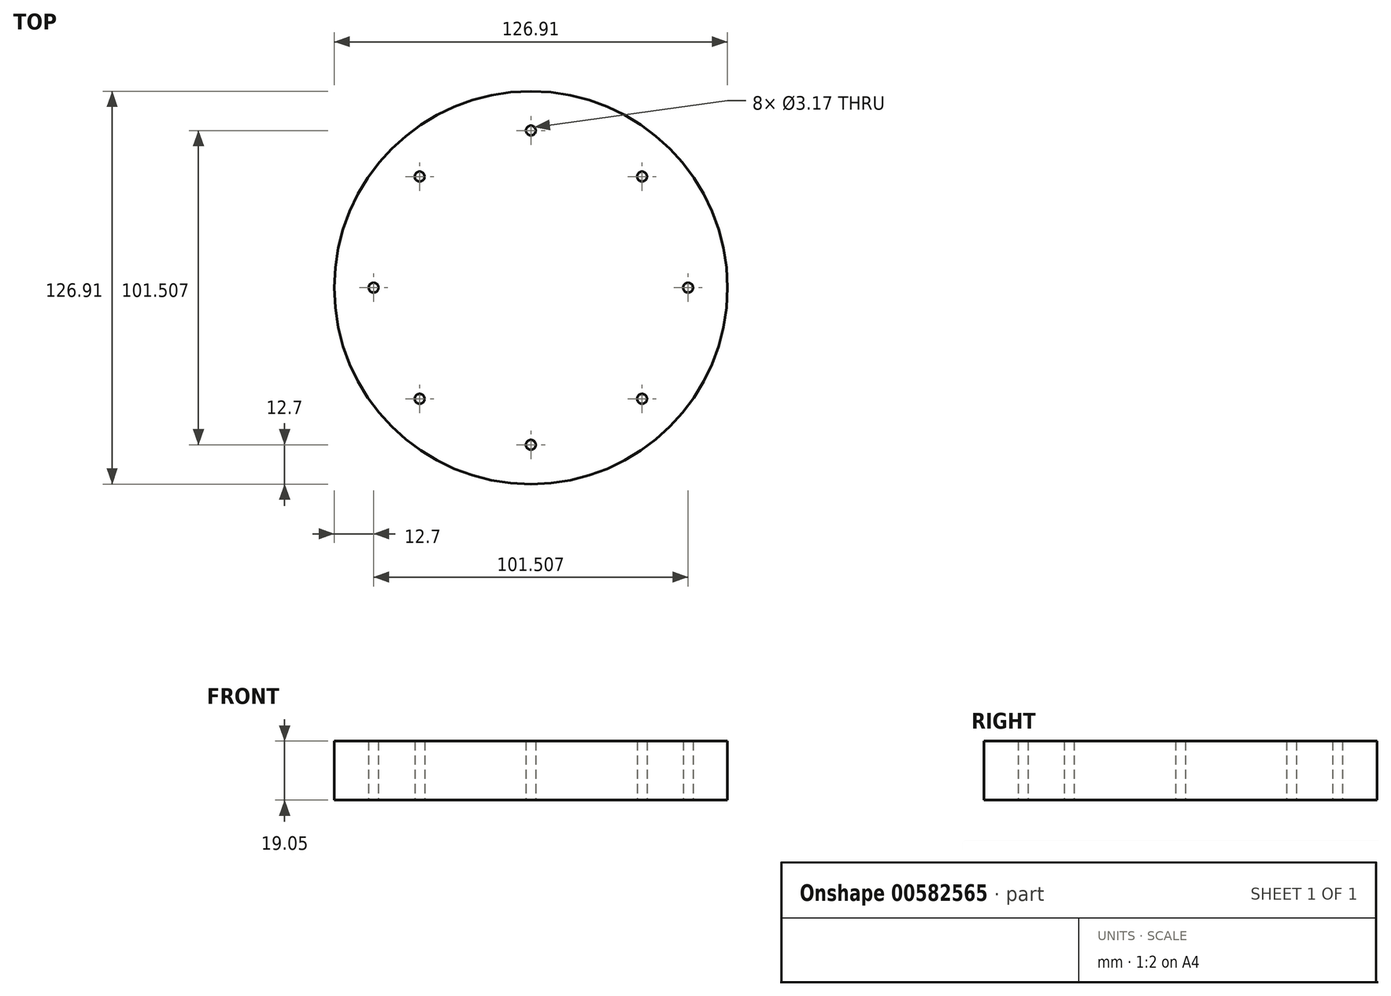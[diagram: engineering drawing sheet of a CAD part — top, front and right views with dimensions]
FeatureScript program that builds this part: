
annotation { "Feature Type Name" : "Feature", "Feature Type Description" : "" }
export const myFeature = defineFeature(function(context is Context, id is Id, definition is map)
    precondition{}
    {
        {
            var Q0;
            Q0=qCreatedBy(makeId("Top.planeOp"),FACE);
            var sketch = newSketch(context, id + "F0", { "sketchPlane" : qUnion([Q0])});
            skCircle(sketch, "E0", {"center": v(76.21, 77.15) * mm, "radius": 63.45 * mm});
            skCircle(sketch, "E1.MirrorC", {"center": v(76.21, 127.9) * mm, "radius": 1.59 * mm});
            skCircle(sketch, "E2.MirrorC", {"center": v(76.21, 26.4) * mm, "radius": 1.59 * mm});
            skCircle(sketch, "E3.MirrorC", {"center": v(25.46, 77.15) * mm, "radius": 1.59 * mm});
            skCircle(sketch, "E4.MirrorC", {"center": v(126.97, 77.15) * mm, "radius": 1.59 * mm});
            skCircle(sketch, "E5.MirrorC", {"center": v(40.33, 113.04) * mm, "radius": 1.59 * mm});
            skCircle(sketch, "E6.MirrorC", {"center": v(112.1, 41.26) * mm, "radius": 1.59 * mm});
            skCircle(sketch, "E7.MirrorC", {"center": v(40.33, 41.26) * mm, "radius": 1.59 * mm});
            skCircle(sketch, "E8.MirrorC", {"center": v(112.1, 113.04) * mm, "radius": 1.59 * mm});
            skSolve(sketch);
        }
        {
            var Q0;
            Q0=makeQuery(id+"F0.imprint","IMPRINT",FACE,{"disambiguationData":[TD([[makeQuery(id+"F0.imprint","IMPRINT",EDGE,{"derivedFrom":sQuery(id+"F0.wireOp",EDGE,"E0")}),1.0]])]});
            extrude(context, id + "F1", {"entities" : qUnion([Q0]), "depth" : 19.05 * mm, "offsetDistance" : 25.4 * mm});
        }
    });
